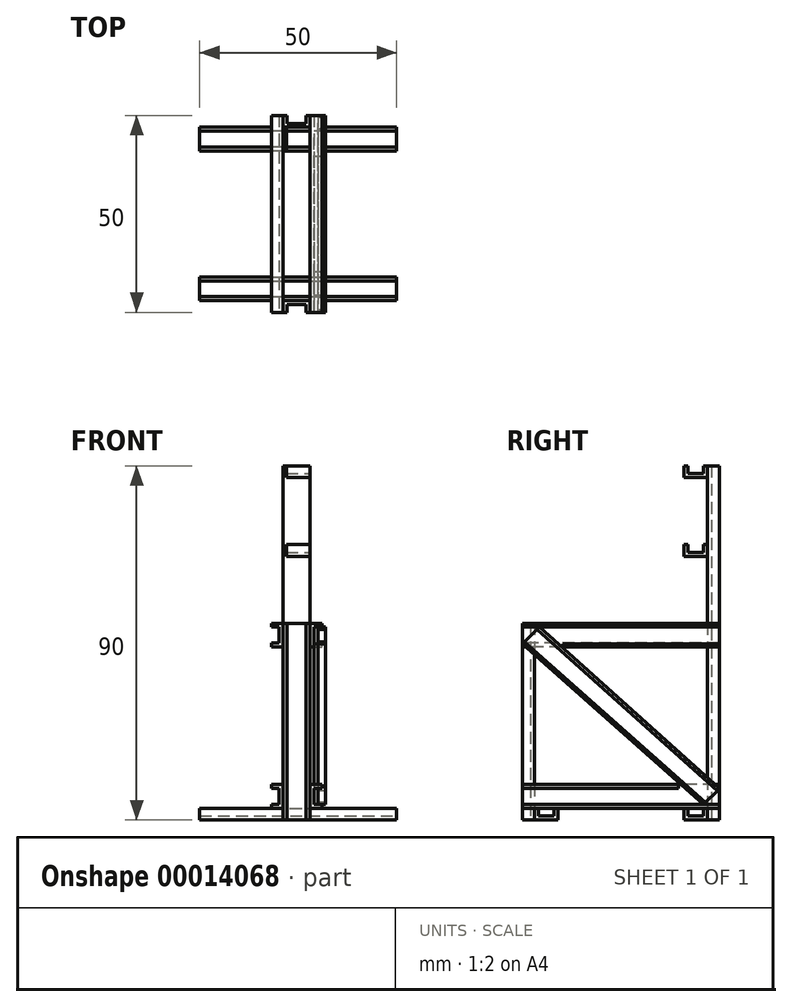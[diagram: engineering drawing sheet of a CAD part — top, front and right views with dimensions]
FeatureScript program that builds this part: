
annotation { "Feature Type Name" : "Feature", "Feature Type Description" : "" }
export const myFeature = defineFeature(function(context is Context, id is Id, definition is map)
    precondition{}
    {
        {
            var Q0;
            Q0=qCreatedBy(makeId("Front.planeOp"),FACE);
            var sketch = newSketch(context, id + "F0", { "sketchPlane" : qUnion([Q0])});
            skLineSegment(sketch, "E0", {"start": v(0, 0) * mm, "end": v(0, 6) * mm});
            skLineSegment(sketch, "E1", {"start": v(0, 6) * mm, "end": v(-3, 6) * mm});
            skLineSegment(sketch, "E2", {"start": v(-3, 6) * mm, "end": v(-3, 5) * mm});
            skLineSegment(sketch, "E3", {"start": v(-3, 5) * mm, "end": v(-1, 5) * mm});
            skLineSegment(sketch, "E4", {"start": v(-1, 5) * mm, "end": v(-1, 1) * mm});
            skLineSegment(sketch, "E5", {"start": v(-1, 1) * mm, "end": v(-3, 1) * mm});
            skLineSegment(sketch, "E6", {"start": v(-3, 1) * mm, "end": v(-3, 0) * mm});
            skLineSegment(sketch, "E7", {"start": v(-3, 0) * mm, "end": v(0, 0) * mm});
            skLineSegment(sketch, "E8", {"start": v(0, 0) * mm, "end": v(6.81, 0) * mm});
            skLineSegment(sketch, "E9", {"start": v(6.81, 0) * mm, "end": v(6.81, 6) * mm});
            skLineSegment(sketch, "E10", {"start": v(6.81, 6) * mm, "end": v(9.81, 6) * mm});
            skLineSegment(sketch, "E11", {"start": v(9.81, 6) * mm, "end": v(9.81, 5) * mm});
            skLineSegment(sketch, "E12", {"start": v(9.81, 5) * mm, "end": v(7.81, 5) * mm});
            skLineSegment(sketch, "E13", {"start": v(7.81, 5) * mm, "end": v(7.81, 1) * mm});
            skLineSegment(sketch, "E14", {"start": v(7.81, 1) * mm, "end": v(9.81, 1) * mm});
            skLineSegment(sketch, "E15", {"start": v(9.81, 1) * mm, "end": v(9.81, 0) * mm});
            skLineSegment(sketch, "E16", {"start": v(9.81, 0) * mm, "end": v(6.81, 0) * mm});
            skSolve(sketch);
        }
        {
            var Q0;
            Q0 = qSketchRegion(id + "F0", true);
            extrude(context, id + "F1", {"entities" : qUnion([Q0]), "oppositeDirection" : true, "depth" : 50 * mm});
        }
        {
            var Q0;
            Q0=makeQuery(id+"F1.opExtrude","SWEPT_FACE",FACE,{"disambiguationData":[OSD([sQuery(id+"F0.wireOp",EDGE,"E16")])]});
            var sketch = newSketch(context, id + "F2", { "sketchPlane" : qUnion([Q0])});
            skLineSegment(sketch, "E17", {"start": v(6.81, 0) * mm, "end": v(6.81, -3) * mm});
            skLineSegment(sketch, "E18", {"start": v(6.81, -3) * mm, "end": v(0, -3) * mm});
            skLineSegment(sketch, "E19", {"start": v(0, -3) * mm, "end": v(0, 0) * mm});
            skLineSegment(sketch, "E20", {"start": v(0, 0) * mm, "end": v(1, 0) * mm});
            skLineSegment(sketch, "E21", {"start": v(1, 0) * mm, "end": v(1, -2) * mm});
            skLineSegment(sketch, "E22", {"start": v(1, -2) * mm, "end": v(5.81, -2) * mm});
            skLineSegment(sketch, "E23", {"start": v(5.81, -2) * mm, "end": v(5.81, 0) * mm});
            skLineSegment(sketch, "E24", {"start": v(5.81, 0) * mm, "end": v(6.81, 0) * mm});
            skSolve(sketch);
        }
        {
            var Q0;
            Q0 = qSketchRegion(id + "F2", true);
            extrude(context, id + "F3", {"entities" : qUnion([Q0]), "oppositeDirection" : true, "depth" : 47 * mm, "hasSecondDirection" : true, "secondDirectionOppositeDirection" : false, "secondDirectionDepth" : 3 * mm});
        }
        {
            var Q0;
            Q0=makeQuery(id+"F1.opExtrude","SWEPT_FACE",FACE,{"disambiguationData":[OSD([sQuery(id+"F0.wireOp",EDGE,"E9")])]});
            var sketch = newSketch(context, id + "F4", { "sketchPlane" : qUnion([Q0])});
            skLineSegment(sketch, "E25", {"start": v(-3, 0) * mm, "end": v(-3, -3) * mm});
            skLineSegment(sketch, "E26", {"start": v(-3, -3) * mm, "end": v(-9, -3) * mm});
            skLineSegment(sketch, "E27", {"start": v(-9, -3) * mm, "end": v(-9, 0) * mm});
            skLineSegment(sketch, "E28", {"start": v(-9, 0) * mm, "end": v(-8, 0) * mm});
            skLineSegment(sketch, "E29", {"start": v(-8, 0) * mm, "end": v(-8, -2) * mm});
            skLineSegment(sketch, "E30", {"start": v(-8, -2) * mm, "end": v(-4, -2) * mm});
            skLineSegment(sketch, "E31", {"start": v(-4, -2) * mm, "end": v(-4, 0) * mm});
            skLineSegment(sketch, "E32", {"start": v(-4, 0) * mm, "end": v(-3, 0) * mm});
            skSolve(sketch);
        }
        {
            var Q0;
            Q0 = qSketchRegion(id + "F4", true);
            extrude(context, id + "F5", {"entities" : qUnion([Q0]), "depth" : 28 * mm, "hasSecondDirection" : true, "secondDirectionOppositeDirection" : true, "secondDirectionDepth" : 22 * mm});
        }
        {
            var Q0;
            Q0=makeQuery(id+"F1.opExtrude","SWEPT_FACE",FACE,{"disambiguationData":[OSD([sQuery(id+"F0.wireOp",EDGE,"E10")])]});
            var sketch = newSketch(context, id + "F6", { "sketchPlane" : qUnion([Q0])});
            skLineSegment(sketch, "E33", {"start": v(6.81, 50) * mm, "end": v(6.81, 47) * mm});
            skLineSegment(sketch, "E34", {"start": v(6.81, 47) * mm, "end": v(0, 47) * mm});
            skLineSegment(sketch, "E35", {"start": v(0, 47) * mm, "end": v(0, 50) * mm});
            skLineSegment(sketch, "E36", {"start": v(0, 50) * mm, "end": v(1, 50) * mm});
            skLineSegment(sketch, "E37", {"start": v(1, 50) * mm, "end": v(1, 48) * mm});
            skLineSegment(sketch, "E38", {"start": v(1, 48) * mm, "end": v(5.81, 48) * mm});
            skLineSegment(sketch, "E39", {"start": v(5.81, 48) * mm, "end": v(5.81, 50) * mm});
            skLineSegment(sketch, "E40", {"start": v(5.81, 50) * mm, "end": v(6.81, 50) * mm});
            skSolve(sketch);
        }
        {
            var Q0;
            Q0 = qSketchRegion(id + "F6", true);
            extrude(context, id + "F7", {"entities" : qUnion([Q0]), "depth" : 81 * mm, "hasSecondDirection" : true, "secondDirectionOppositeDirection" : true, "secondDirectionDepth" : 9 * mm});
        }
        {
            var Q0;
            Q0=makeQuery(id+"F7.opExtrude","SWEPT_FACE",FACE,{"disambiguationData":[OSD([sQuery(id+"F6.wireOp",EDGE,"E33")])]});
            var sketch = newSketch(context, id + "F8", { "sketchPlane" : qUnion([Q0])});
            skLineSegment(sketch, "E41", {"start": v(47, -3) * mm, "end": v(41, -3) * mm});
            skLineSegment(sketch, "E42", {"start": v(41, -3) * mm, "end": v(41, 0) * mm});
            skLineSegment(sketch, "E43", {"start": v(41, 0) * mm, "end": v(42, 0) * mm});
            skLineSegment(sketch, "E44", {"start": v(42, 0) * mm, "end": v(42, -2) * mm});
            skLineSegment(sketch, "E45", {"start": v(42, -2) * mm, "end": v(46, -2) * mm});
            skLineSegment(sketch, "E46", {"start": v(46, -2) * mm, "end": v(46, 0) * mm});
            skLineSegment(sketch, "E47", {"start": v(46, 0) * mm, "end": v(47, 0) * mm});
            skLineSegment(sketch, "E48", {"start": v(47, 0) * mm, "end": v(47, -3) * mm});
            skSolve(sketch);
        }
        {
            var Q0;
            Q0 = qSketchRegion(id + "F8", true);
            extrude(context, id + "F9", {"entities" : qUnion([Q0]), "depth" : 22 * mm, "hasSecondDirection" : true, "secondDirectionOppositeDirection" : true, "secondDirectionDepth" : 28 * mm});
        }
        {
            var Q0;
            Q0=makeQuery(id+"F3.opExtrude","SWEPT_FACE",FACE,{"disambiguationData":[OSD([sQuery(id+"F2.wireOp",EDGE,"E20")])]});
            var sketch = newSketch(context, id + "F10", { "sketchPlane" : qUnion([Q0])});
            skLineSegment(sketch, "E49", {"start": v(0, 47) * mm, "end": v(0, 41) * mm});
            skLineSegment(sketch, "E50", {"start": v(0, 41) * mm, "end": v(-3, 41) * mm});
            skLineSegment(sketch, "E51", {"start": v(-3, 41) * mm, "end": v(-3, 42) * mm});
            skLineSegment(sketch, "E52", {"start": v(-3, 42) * mm, "end": v(-1, 42) * mm});
            skLineSegment(sketch, "E53", {"start": v(-1, 42) * mm, "end": v(-1, 46) * mm});
            skLineSegment(sketch, "E54", {"start": v(-1, 46) * mm, "end": v(-3, 46) * mm});
            skLineSegment(sketch, "E55", {"start": v(-3, 46) * mm, "end": v(-3, 47) * mm});
            skLineSegment(sketch, "E56", {"start": v(-3, 47) * mm, "end": v(0, 47) * mm});
            skLineSegment(sketch, "E57", {"start": v(0, 41) * mm, "end": v(0, 47) * mm});
            skLineSegment(sketch, "E58", {"start": v(1, 47) * mm, "end": v(6.81, 47) * mm});
            skLineSegment(sketch, "E59", {"start": v(6.81, 47) * mm, "end": v(6.81, 41) * mm});
            skLineSegment(sketch, "E60", {"start": v(6.81, 41) * mm, "end": v(9.81, 41) * mm});
            skLineSegment(sketch, "E61", {"start": v(9.81, 41) * mm, "end": v(9.81, 41.74) * mm});
            skLineSegment(sketch, "E62", {"start": v(9.81, 41.74) * mm, "end": v(7.81, 41.74) * mm});
            skLineSegment(sketch, "E63", {"start": v(7.81, 41.74) * mm, "end": v(7.81, 46) * mm});
            skLineSegment(sketch, "E64", {"start": v(7.81, 46) * mm, "end": v(9.81, 46) * mm});
            skLineSegment(sketch, "E65", {"start": v(9.81, 46) * mm, "end": v(9.81, 47) * mm});
            skLineSegment(sketch, "E66", {"start": v(9.81, 47) * mm, "end": v(6.81, 47) * mm});
            skSolve(sketch);
        }
        {
            var Q0;
            Q0 = qSketchRegion(id + "F10", true);
            extrude(context, id + "F11", {"entities" : qUnion([Q0]), "oppositeDirection" : true, "depth" : 50 * mm});
        }
        {
            var Q0;
            Q0=makeQuery(id+"F7.opExtrude","SWEPT_FACE",FACE,{"disambiguationData":[OSD([sQuery(id+"F6.wireOp",EDGE,"E33")])]});
            var sketch = newSketch(context, id + "F12", { "sketchPlane" : qUnion([Q0])});
            skLineSegment(sketch, "E67", {"start": v(47, 87) * mm, "end": v(47, 84) * mm});
            skLineSegment(sketch, "E68", {"start": v(47, 84) * mm, "end": v(41, 84) * mm});
            skLineSegment(sketch, "E69", {"start": v(41, 84) * mm, "end": v(41, 87) * mm});
            skLineSegment(sketch, "E70", {"start": v(41, 87) * mm, "end": v(42, 87) * mm});
            skLineSegment(sketch, "E71", {"start": v(42, 87) * mm, "end": v(42, 85) * mm});
            skLineSegment(sketch, "E72", {"start": v(42, 85) * mm, "end": v(46, 85) * mm});
            skLineSegment(sketch, "E73", {"start": v(46, 85) * mm, "end": v(46, 87) * mm});
            skLineSegment(sketch, "E74", {"start": v(46, 87) * mm, "end": v(47, 87) * mm});
            skLineSegment(sketch, "E75", {"start": v(47, 84) * mm, "end": v(47, 87) * mm});
            skLineSegment(sketch, "E76", {"start": v(47, 67) * mm, "end": v(46, 67) * mm});
            skLineSegment(sketch, "E77", {"start": v(46, 67) * mm, "end": v(46, 65) * mm});
            skLineSegment(sketch, "E78", {"start": v(46, 65) * mm, "end": v(42, 65) * mm});
            skLineSegment(sketch, "E79", {"start": v(42, 65) * mm, "end": v(42, 67) * mm});
            skLineSegment(sketch, "E80", {"start": v(42, 67) * mm, "end": v(41, 67) * mm});
            skLineSegment(sketch, "E81", {"start": v(41, 67) * mm, "end": v(41, 64) * mm});
            skLineSegment(sketch, "E82", {"start": v(41, 64) * mm, "end": v(47, 64) * mm});
            skLineSegment(sketch, "E83", {"start": v(47, 64) * mm, "end": v(47, 67) * mm});
            skSolve(sketch);
        }
        {
            var Q0;
            Q0 = qSketchRegion(id + "F12", true);
            extrude(context, id + "F13", {"entities" : qUnion([Q0]), "oppositeDirection" : true, "depth" : 6 * mm});
        }
        {
            var Q0;
            Q0=makeQuery(id+"F1.opExtrude","SWEPT_FACE",FACE,{"disambiguationData":[OSD([sQuery(id+"F0.wireOp",EDGE,"E13")])]});
            var sketch = newSketch(context, id + "F14", { "sketchPlane" : qUnion([Q0])});
            skLineSegment(sketch, "E84", {"start": v(50, 5) * mm, "end": v(46, 1) * mm});
            skLineSegment(sketch, "E85", {"start": v(0, 41.76) * mm, "end": v(4.26, 46.02) * mm});
            skLineSegment(sketch, "E86", {"start": v(0, 41.76) * mm, "end": v(46, 1) * mm});
            skLineSegment(sketch, "E87", {"start": v(50, 5) * mm, "end": v(4.26, 46.02) * mm});
            skSolve(sketch);
        }
        {
            var Q0;
            Q0 = qSketchRegion(id + "F14", true);
            extrude(context, id + "F15", {"entities" : qUnion([Q0]), "depth" : 1 * mm});
        }
        {
            var Q0;
            Q0=makeQuery(id+"F15.opExtrude","CAP_FACE",FACE,{"disambiguationData":[OSD([sQuery(id+"F14.wireOp",EDGE,"E84"),sQuery(id+"F14.wireOp",EDGE,"E85"),sQuery(id+"F14.wireOp",EDGE,"E86"),sQuery(id+"F14.wireOp",EDGE,"E87")])],"isStart":false});
            var sketch = newSketch(context, id + "F16", { "sketchPlane" : qUnion([Q0])});
            skLineSegment(sketch, "E88", {"start": v(4.26, 46.02) * mm, "end": v(3.71, 45.47) * mm});
            skLineSegment(sketch, "E89", {"start": v(3.71, 45.47) * mm, "end": v(49.46, 4.46) * mm});
            skLineSegment(sketch, "E90", {"start": v(46.53, 1.53) * mm, "end": v(0.53, 42.29) * mm});
            skSolve(sketch);
        }
        {
            var Q0;
            Q0=makeQuery(id+"F16.imprint","IMPRINT",FACE,{"disambiguationData":[TD([[makeQuery(id+"F16.imprint","IMPRINT",EDGE,{"derivedFrom":sQuery(id+"F16.wireOp",EDGE,"E88")}),-1.0]])]});
            var Q1;
            {var subQ1=sQuery(id+"F16.wireOp",EDGE,"E90");Q1=makeQuery(id+"F16.imprint","IMPRINT",FACE,{"disambiguationData":[TD([[makeQuery(id+"F16.imprint","IMPRINT",EDGE,{"derivedFrom":subQ1}),1.0]])]});}
            extrude(context, id + "F17", {"entities" : qUnion([Q0, Q1]), "depth" : 2 * mm});
        }
        {
            var Q0;
            Q0=makeQuery(id+"F11.opExtrude","SWEPT_FACE",FACE,{"disambiguationData":[OSD([sQuery(id+"F10.wireOp",EDGE,"E61")])]});
            var sketch = newSketch(context, id + "F18", { "sketchPlane" : qUnion([Q0])});
            skLineSegment(sketch, "E91", {"start": v(10.3, 41) * mm, "end": v(10.3, 41.74) * mm});
            skSolve(sketch);
        }
        {
            var Q0;
            {var subQ2=sQuery(id+"F18.wireOp",EDGE,"E91");Q0=makeQuery(id+"F18.imprint","IMPRINT",FACE,{"disambiguationData":[TD([[makeQuery(id+"F18.imprint","IMPRINT",EDGE,{"derivedFrom":subQ2}),1.0]])]});}
            extrude(context, id + "F19", {"entities" : qUnion([Q0]), "oppositeDirection" : true, "depth" : 2 * mm});
        }
        {
            var Q0;
            Q0=makeQuery(id+"F19.opExtrude","SWEPT_BODY",BODY,{"disambiguationData":[OSD([sQuery(id+"F10.wireOp",EDGE,"E60"),sQuery(id+"F10.wireOp",EDGE,"E61"),sQuery(id+"F10.wireOp",EDGE,"E62"),sQuery(id+"F18.wireOp",EDGE,"E91")])]});
            var Q1;
            Q1=makeQuery(id+"F11.opExtrude","SWEPT_BODY",BODY,{"disambiguationData":[OSD([sQuery(id+"F10.wireOp",EDGE,"E59"),sQuery(id+"F10.wireOp",EDGE,"E60"),sQuery(id+"F10.wireOp",EDGE,"E61"),sQuery(id+"F10.wireOp",EDGE,"E62"),sQuery(id+"F10.wireOp",EDGE,"E63"),sQuery(id+"F10.wireOp",EDGE,"E64"),sQuery(id+"F10.wireOp",EDGE,"E65"),sQuery(id+"F10.wireOp",EDGE,"E66")])]});
            booleanBodies(context, id + "F20", {"operationType" : BooleanOperationType.SUBTRACTION, "tools" : qUnion([Q0]), "targets" : qUnion([Q1])});
        }
        {
            var Q0;
            Q0=makeQuery(id+"F1.opExtrude","SWEPT_FACE",FACE,{"disambiguationData":[OSD([sQuery(id+"F0.wireOp",EDGE,"E11")])]});
            var sketch = newSketch(context, id + "F21", { "sketchPlane" : qUnion([Q0])});
            skLineSegment(sketch, "E92", {"start": v(39.65, 6) * mm, "end": v(39.65, 5) * mm});
            skSolve(sketch);
        }
        {
            var Q0;
            {var subQ2=sQuery(id+"F21.wireOp",EDGE,"E92");Q0=makeQuery(id+"F21.imprint","IMPRINT",FACE,{"disambiguationData":[TD([[makeQuery(id+"F21.imprint","IMPRINT",EDGE,{"derivedFrom":subQ2}),1.0]])]});}
            extrude(context, id + "F22", {"entities" : qUnion([Q0]), "oppositeDirection" : true, "depth" : 2 * mm});
        }
        {
            var Q0;
            Q0=makeQuery(id+"F22.opExtrude","SWEPT_BODY",BODY,{"disambiguationData":[OSD([sQuery(id+"F0.wireOp",EDGE,"E10"),sQuery(id+"F0.wireOp",EDGE,"E11"),sQuery(id+"F0.wireOp",EDGE,"E12"),sQuery(id+"F21.wireOp",EDGE,"E92")])]});
            var Q1;
            Q1=makeQuery(id+"F1.opExtrude","SWEPT_BODY",BODY,{"disambiguationData":[OSD([sQuery(id+"F0.wireOp",EDGE,"E9"),sQuery(id+"F0.wireOp",EDGE,"E10"),sQuery(id+"F0.wireOp",EDGE,"E11"),sQuery(id+"F0.wireOp",EDGE,"E12"),sQuery(id+"F0.wireOp",EDGE,"E13"),sQuery(id+"F0.wireOp",EDGE,"E14"),sQuery(id+"F0.wireOp",EDGE,"E15"),sQuery(id+"F0.wireOp",EDGE,"E16")])]});
            booleanBodies(context, id + "F23", {"operationType" : BooleanOperationType.SUBTRACTION, "tools" : qUnion([Q0]), "targets" : qUnion([Q1])});
        }
        {
            var Q0;
            Q0=makeQuery(id+"F7.opExtrude","SWEPT_BODY",BODY,{"disambiguationData":[OSD([sQuery(id+"F6.wireOp",EDGE,"E33"),sQuery(id+"F6.wireOp",EDGE,"E34"),sQuery(id+"F6.wireOp",EDGE,"E35"),sQuery(id+"F6.wireOp",EDGE,"E36"),sQuery(id+"F6.wireOp",EDGE,"E37"),sQuery(id+"F6.wireOp",EDGE,"E38"),sQuery(id+"F6.wireOp",EDGE,"E39"),sQuery(id+"F6.wireOp",EDGE,"E40")])]});
            var Q1;
            Q1=makeQuery(id+"F11.opExtrude","SWEPT_BODY",BODY,{"disambiguationData":[OSD([sQuery(id+"F10.wireOp",EDGE,"E50"),sQuery(id+"F10.wireOp",EDGE,"E51"),sQuery(id+"F10.wireOp",EDGE,"E52"),sQuery(id+"F10.wireOp",EDGE,"E53"),sQuery(id+"F10.wireOp",EDGE,"E54"),sQuery(id+"F10.wireOp",EDGE,"E55"),sQuery(id+"F10.wireOp",EDGE,"E56"),sQuery(id+"F10.wireOp",EDGE,"E57")])]});
            booleanBodies(context, id + "F24", {"operationType" : BooleanOperationType.UNION, "tools" : qUnion([Q0, Q1])});
        }
        {
            var Q0;
            Q0=makeQuery(id+"F24.opBoolean","MERGE",FACE,{"derivedFrom":[makeQuery(id+"F7.opExtrude","SWEPT_FACE",FACE,{"disambiguationData":[OSD([sQuery(id+"F6.wireOp",EDGE,"E36")])]}),makeQuery(id+"F11.opExtrude","CAP_FACE",FACE,{"disambiguationData":[OSD([sQuery(id+"F10.wireOp",EDGE,"E50"),sQuery(id+"F10.wireOp",EDGE,"E51"),sQuery(id+"F10.wireOp",EDGE,"E52"),sQuery(id+"F10.wireOp",EDGE,"E53"),sQuery(id+"F10.wireOp",EDGE,"E54"),sQuery(id+"F10.wireOp",EDGE,"E55"),sQuery(id+"F10.wireOp",EDGE,"E56"),sQuery(id+"F10.wireOp",EDGE,"E57")])],"isStart":false})]});
            var sketch = newSketch(context, id + "F25", { "sketchPlane" : qUnion([Q0])});
            skLineSegment(sketch, "E93", {"start": v(0, 0) * mm, "end": v(3, 0) * mm});
            skLineSegment(sketch, "E94", {"start": v(3, 0) * mm, "end": v(3, 1) * mm});
            skLineSegment(sketch, "E95", {"start": v(3, 1) * mm, "end": v(1, 1) * mm});
            skLineSegment(sketch, "E96", {"start": v(1, 1) * mm, "end": v(1, 5) * mm});
            skLineSegment(sketch, "E97", {"start": v(1, 5) * mm, "end": v(3, 5) * mm});
            skLineSegment(sketch, "E98", {"start": v(3, 5) * mm, "end": v(3, 6) * mm});
            skLineSegment(sketch, "E99", {"start": v(3, 6) * mm, "end": v(0, 6) * mm});
            skLineSegment(sketch, "E100", {"start": v(0, 6) * mm, "end": v(0, 0) * mm});
            skSolve(sketch);
        }
        {
            var Q0;
            Q0=makeQuery(id+"F25.imprint","IMPRINT",FACE,{"disambiguationData":[TD([[makeQuery(id+"F25.imprint","IMPRINT",EDGE,{"derivedFrom":sQuery(id+"F25.wireOp",EDGE,"E93")}),1.0]])]});
            extrude(context, id + "F26", {"entities" : qUnion([Q0]), "oppositeDirection" : true, "depth" : 50 * mm});
        }
    });
